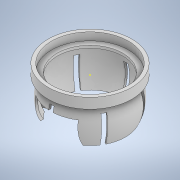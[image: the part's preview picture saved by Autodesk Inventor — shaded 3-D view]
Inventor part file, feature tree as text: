
AUTODESK INVENTOR PART (.ipt)
format: ipt  version: 2022 (Build 260153000, 153)  size: 226,304 bytes
history: native  units: in
note: dims shown in document units (in); Inventor stores cm internally (conversion verified against a paired STEP export)
features: other x3, sketch x3, extrude x2
ambient origin geometry x8: Origin, YZ Plane, XZ Plane, XY Plane, X Axis, Y Axis, Z Axis, Center Point
bodies: Solid1 (feature_tree)
feature tree (8):
  other  "cam-socket-try1.ipt"
  sketch  "Sketch1"  dims[d0=0.3937in d2=3.8268in]
  extrude  "Extrusion1"  Depth=0.3937in
  extrude  "Extrusion2"  Depth=0.1181in
  other  "Solid1::cam-socket-try1.ipt"
  other  "TaggingFeature1"
  sketch  "Sketch2"  dims[d3=0.1181in d4=0.0in d5=0.1575in]
  sketch  "Sketch3"  dims[d6=0.3543in d7=0.0in]
